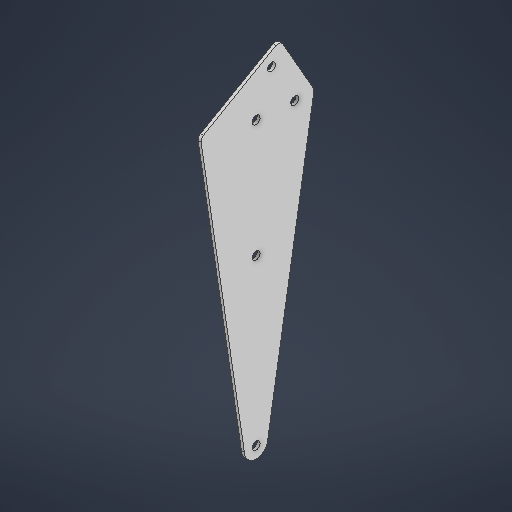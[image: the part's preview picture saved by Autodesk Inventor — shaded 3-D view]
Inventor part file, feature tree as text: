
AUTODESK INVENTOR PART (.ipt)
format: ipt  version: 2025.2 (Build 292293000, 293)  size: 201,216 bytes
history: native  units: in
note: dims shown in document units (in); Inventor stores cm internally (conversion verified against a paired STEP export)
features: extrude x1, sketch x1
ambient origin geometry x8: Origin, YZ Plane, XZ Plane, XY Plane, X Axis, Y Axis, Z Axis, Center Point
bodies: Solid1 (feature_tree)
feature tree (2):
  extrude  "Extrusion1"  Depth=0.0625in TaperAngle=0.0deg
  sketch  "Sketch1"  dims[d0=0.5in d1=0.125in d2=0.1in d3=0.0625in d4=0.0in d5=0.5in d6=0.0344in]
